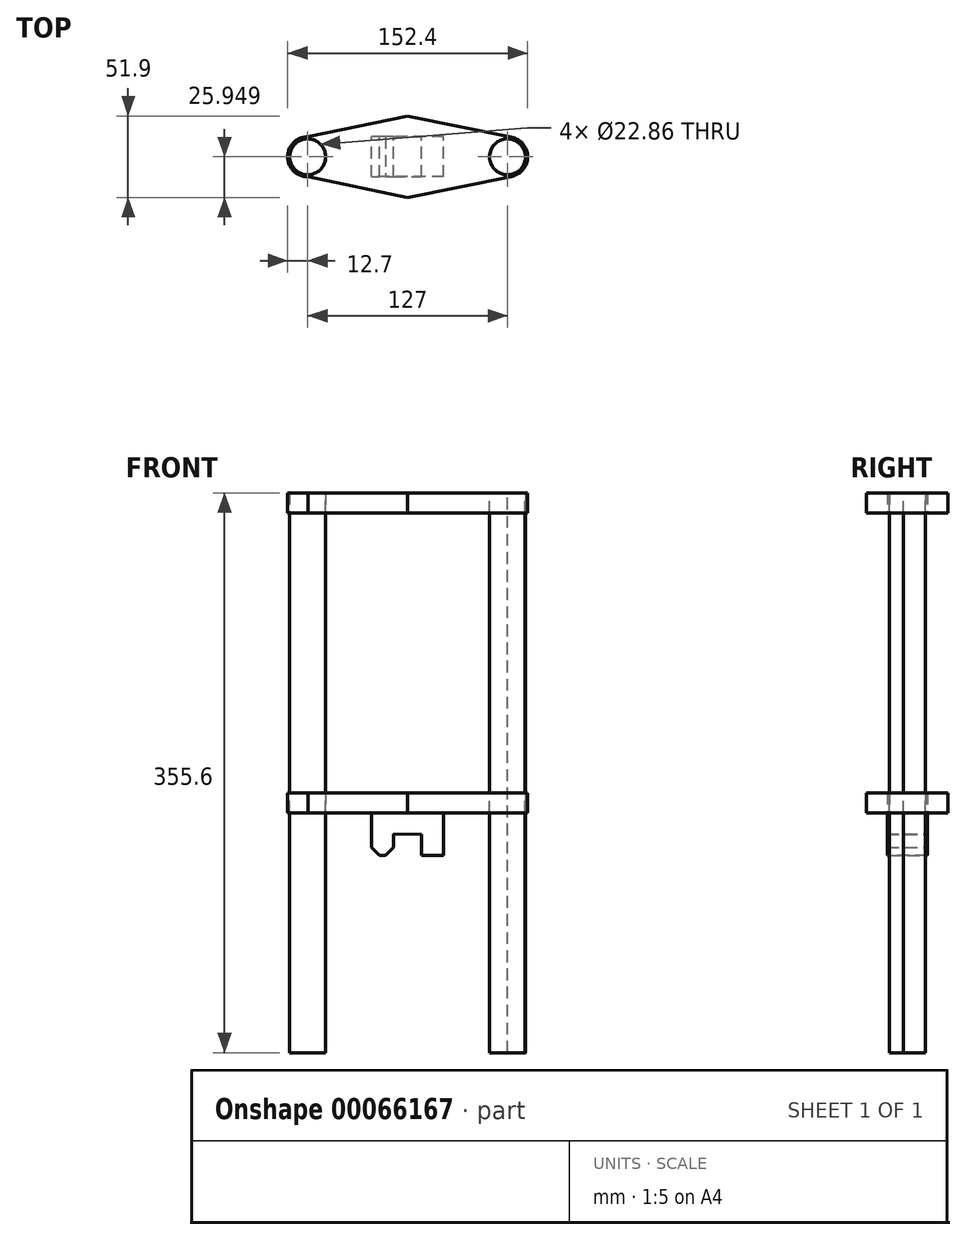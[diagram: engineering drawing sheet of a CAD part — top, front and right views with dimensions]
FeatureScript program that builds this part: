
annotation { "Feature Type Name" : "Feature", "Feature Type Description" : "" }
export const myFeature = defineFeature(function(context is Context, id is Id, definition is map)
    precondition{}
    {
        {
            var Q0;
            Q0=qCreatedBy(makeId("Top.planeOp"),FACE);
            var sketch = newSketch(context, id + "F0", { "sketchPlane" : qUnion([Q0])});
            skCircle(sketch, "E0", {"center": v(-63.5, 0) * mm, "radius": 12.7 * mm});
            skCircle(sketch, "E1", {"center": v(63.5, 0) * mm, "radius": 12.7 * mm});
            skLineSegment(sketch, "E2", {"start": v(-63.25, 12.7) * mm, "end": v(0, 25.95) * mm});
            skLineSegment(sketch, "E3", {"start": v(-63.25, -12.7) * mm, "end": v(0, -25.95) * mm});
            skLineSegment(sketch, "E4", {"start": v(0, -25.95) * mm, "end": v(66.05, -12.44) * mm});
            skLineSegment(sketch, "E5", {"start": v(0, 25.95) * mm, "end": v(66.04, 12.44) * mm});
            skCircle(sketch, "E6", {"center": v(-63.5, 0) * mm, "radius": 11.43 * mm});
            skCircle(sketch, "E7", {"center": v(63.5, 0) * mm, "radius": 11.43 * mm});
            skSolve(sketch);
        }
        {
            var Q0;
            Q0=makeQuery(id+"F0.imprint","IMPRINT",FACE,{"disambiguationData":[TD([[makeQuery(id+"F0.imprint","IMPRINT",EDGE,{"derivedFrom":sQuery(id+"F0.wireOp",EDGE,"E7")}),-1.0]])]});
            var Q1;
            Q1=makeQuery(id+"F0.imprint","IMPRINT",FACE,{"disambiguationData":[TD([[makeQuery(id+"F0.imprint","IMPRINT",EDGE,{"derivedFrom":sQuery(id+"F0.wireOp",EDGE,"E6")}),-1.0]])]});
            var Q2;
            {var subQ0=sQuery(id+"F0.wireOp",EDGE,"E2");Q2=makeQuery(id+"F0.imprint","IMPRINT",FACE,{"disambiguationData":[TD([[makeQuery(id+"F0.imprint","IMPRINT",EDGE,{"derivedFrom":subQ0}),-1.0]])]});}
            extrude(context, id + "F1", {"entities" : qUnion([Q0, Q1, Q2]), "endBound" : BoundingType.SYMMETRIC, "depth" : 12.7 * mm});
        }
        {
            var Q0;
            Q0=makeQuery(id+"F1.opExtrude","SWEPT_BODY",BODY,{"disambiguationData":[OSD([sQuery(id+"F0.wireOp",EDGE,"E0"),sQuery(id+"F0.wireOp",EDGE,"E1"),sQuery(id+"F0.wireOp",EDGE,"E2"),sQuery(id+"F0.wireOp",EDGE,"E3"),sQuery(id+"F0.wireOp",EDGE,"E4"),sQuery(id+"F0.wireOp",EDGE,"E5"),sQuery(id+"F0.wireOp",EDGE,"E6"),sQuery(id+"F0.wireOp",EDGE,"E7")])]});
            transform(context, id + "F2", {"entities" : qUnion([Q0]), "transformType" : TransformType.TRANSLATION_3D, "dx" : 0 * mm, "dy" : 0 * mm, "dz" : 0 * mm, "makeCopy" : true});
        }
        {
            var Q0;
            Q0=makeQuery(id+"F2.opPattern","COPY",BODY,{"derivedFrom":makeQuery(id+"F1.opExtrude","SWEPT_BODY",BODY,{"disambiguationData":[OSD([sQuery(id+"F0.wireOp",EDGE,"E0"),sQuery(id+"F0.wireOp",EDGE,"E1"),sQuery(id+"F0.wireOp",EDGE,"E2"),sQuery(id+"F0.wireOp",EDGE,"E3"),sQuery(id+"F0.wireOp",EDGE,"E4"),sQuery(id+"F0.wireOp",EDGE,"E5"),sQuery(id+"F0.wireOp",EDGE,"E6"),sQuery(id+"F0.wireOp",EDGE,"E7")])]}),"instanceName":"1"});
            deleteBodies(context, id + "F3", {"entities" : qUnion([Q0])});
        }
        {
            var Q0;
            Q0=makeQuery(id+"F1.opExtrude","SWEPT_BODY",BODY,{"disambiguationData":[OSD([sQuery(id+"F0.wireOp",EDGE,"E0"),sQuery(id+"F0.wireOp",EDGE,"E1"),sQuery(id+"F0.wireOp",EDGE,"E2"),sQuery(id+"F0.wireOp",EDGE,"E3"),sQuery(id+"F0.wireOp",EDGE,"E4"),sQuery(id+"F0.wireOp",EDGE,"E5"),sQuery(id+"F0.wireOp",EDGE,"E6"),sQuery(id+"F0.wireOp",EDGE,"E7")])]});
            transform(context, id + "F4", {"entities" : qUnion([Q0]), "transformType" : TransformType.TRANSLATION_3D, "dx" : 0 * mm, "dy" : 0 * mm, "dz" : 190.5 * mm, "makeCopy" : true});
        }
        {
            var Q0;
            Q0=makeQuery(id+"F4.opPattern","COPY",FACE,{"derivedFrom":makeQuery(id+"F1.opExtrude","CAP_FACE",FACE,{"disambiguationData":[OSD([sQuery(id+"F0.wireOp",EDGE,"E0"),sQuery(id+"F0.wireOp",EDGE,"E1"),sQuery(id+"F0.wireOp",EDGE,"E2"),sQuery(id+"F0.wireOp",EDGE,"E3"),sQuery(id+"F0.wireOp",EDGE,"E4"),sQuery(id+"F0.wireOp",EDGE,"E5"),sQuery(id+"F0.wireOp",EDGE,"E6"),sQuery(id+"F0.wireOp",EDGE,"E7")])],"isStart":false}),"instanceName":"1"});
            var sketch = newSketch(context, id + "F5", { "sketchPlane" : qUnion([Q0])});
            skPoint(sketch, "E8.first.point", {"position": v(-63.25, 11.43) * mm});
            skPoint(sketch, "E8.second.point", {"position": v(-63.25, -11.43) * mm});
            skPoint(sketch, "E8.third.point", {"position": v(-52.07, 0) * mm});
            skPoint(sketch, "E9.first.point", {"position": v(63.58, 11.43) * mm});
            skPoint(sketch, "E9.second.point", {"position": v(64.02, -11.42) * mm});
            skPoint(sketch, "E9.third.point", {"position": v(52.07, 0) * mm});
            skPoint(sketch, "E9.third.point.positionSnap0", {"position": v(76.2, 0) * mm});
            skCircle(sketch, "E10", {"center": v(63.15, -0.28) * mm, "radius": 11.71 * mm});
            skPoint(sketch, "E10.second.point", {"position": v(63.58, -11.98) * mm});
            skPoint(sketch, "E10.third.point", {"position": v(74.66, -2.49) * mm});
            skCircle(sketch, "E11", {"center": v(-63.4, -0.16) * mm, "radius": 11.59 * mm});
            skPoint(sketch, "E11.second.point", {"position": v(-63.25, -11.74) * mm});
            skPoint(sketch, "E11.third.point", {"position": v(-55.47, -8.61) * mm});
            skSolve(sketch);
        }
        {
            var Q0;
            Q0=makeQuery(id+"F5.imprint","IMPRINT",FACE,{"disambiguationData":[TD([[makeQuery(id+"F5.imprint","IMPRINT",EDGE,{"derivedFrom":sQuery(id+"F5.wireOp",EDGE,"E8")}),1.0]])]});
            var Q1;
            Q1=makeQuery(id+"F5.imprint","IMPRINT",FACE,{"disambiguationData":[TD([[makeQuery(id+"F5.imprint","IMPRINT",EDGE,{"derivedFrom":sQuery(id+"F5.wireOp",EDGE,"E9")}),1.0]])]});
            var Q2;
            {var subQ0=sQuery(id+"F5.wireOp",EDGE,"E10");var subQ1=makeQuery(id+"F4.opPattern","COPY",EDGE,{"derivedFrom":makeQuery(id+"F1.opExtrude","CAP_EDGE",EDGE,{"disambiguationData":[OSD([sQuery(id+"F0.wireOp",EDGE,"E7")])],"isStart":false}),"instanceName":"1"});var subQ2=makeQuery(id+"F5.imprint","INTERSECT",VERTEX,{"disambiguationData":[OD(0.0)],"derivedFrom":[subQ1,subQ0]});Q2=makeQuery(id+"F5.imprint","IMPRINT",FACE,{"disambiguationData":[TD([[makeQuery(id+"F5.imprint","IMPRINT",EDGE,{"disambiguationData":[TD([[subQ2,1.0]])],"derivedFrom":subQ0}),1.0]])]});}
            var Q3;
            {var subQ0=sQuery(id+"F5.wireOp",EDGE,"E11");var subQ1=makeQuery(id+"F4.opPattern","COPY",EDGE,{"derivedFrom":makeQuery(id+"F1.opExtrude","CAP_EDGE",EDGE,{"disambiguationData":[OSD([sQuery(id+"F0.wireOp",EDGE,"E6")])],"isStart":false}),"instanceName":"1"});var subQ2=makeQuery(id+"F5.imprint","INTERSECT",VERTEX,{"disambiguationData":[OD(0.0)],"derivedFrom":[subQ1,subQ0]});Q3=makeQuery(id+"F5.imprint","IMPRINT",FACE,{"disambiguationData":[TD([[makeQuery(id+"F5.imprint","IMPRINT",EDGE,{"disambiguationData":[TD([[subQ2,1.0]])],"derivedFrom":subQ0}),1.0]])]});}
            extrude(context, id + "F6", {"entities" : qUnion([Q0, Q1, Q2, Q3]), "oppositeDirection" : true, "depth" : 355.6 * mm});
        }
        {
            var Q0;
            Q0=qCreatedBy(makeId("Front.planeOp"),FACE);
            var sketch = newSketch(context, id + "F7", { "sketchPlane" : qUnion([Q0])});
            skLineSegment(sketch, "E12.rect.bottom", {"start": v(22.86, -6.47) * mm, "end": v(-22.86, -6.47) * mm});
            skLineSegment(sketch, "E12.rect.top", {"start": v(22.86, -33.55) * mm, "end": v(-22.86, -33.55) * mm});
            skLineSegment(sketch, "E12.rect.left", {"start": v(22.86, -6.47) * mm, "end": v(22.86, -33.55) * mm});
            skLineSegment(sketch, "E12.rect.right", {"start": v(-22.86, -6.47) * mm, "end": v(-22.86, -33.55) * mm});
            skPoint(sketch, "E12.rect.middle", {"position": v(0, -20.01) * mm});
            skLineSegment(sketch, "E13", {"start": v(-8.9, -33.55) * mm, "end": v(-8.9, -19.86) * mm});
            skLineSegment(sketch, "E14", {"start": v(-8.9, -19.86) * mm, "end": v(9.27, -20.01) * mm});
            skLineSegment(sketch, "E15", {"start": v(8.9, -33.55) * mm, "end": v(8.9, -20) * mm});
            skPoint(sketch, "E16.start.orphan", {"position": v(0, -33.55) * mm});
            skSolve(sketch);
        }
        {
            var Q0;
            Q0=makeQuery(id+"F7.imprint","IMPRINT",FACE,{"disambiguationData":[TD([[makeQuery(id+"F7.imprint","IMPRINT",EDGE,{"derivedFrom":sQuery(id+"F7.wireOp",EDGE,"E12.rect.bottom")}),1.0]])]});
            extrude(context, id + "F8", {"entities" : qUnion([Q0]), "endBound" : BoundingType.SYMMETRIC, "depth" : 25.4 * mm});
        }
        {
            var Q0;
            Q0=makeQuery(id+"F8.opExtrude","SWEPT_EDGE",EDGE,{"disambiguationData":[OSD([sQuery(id+"F7.wireOp",EDGE,"E12.rect.top"),sQuery(id+"F7.wireOp",EDGE,"E13")])]});
            var Q1;
            Q1=makeQuery(id+"F8.opExtrude","SWEPT_EDGE",EDGE,{"disambiguationData":[OSD([sQuery(id+"F7.wireOp",EDGE,"E12.rect.top"),sQuery(id+"F7.wireOp",EDGE,"E12.rect.right")])]});
            chamfer(context, id + "F9", {"entities" : qUnion([Q0, Q1]), "width" : 5.08 * mm, "tangentPropagation" : true});
        }
    });
